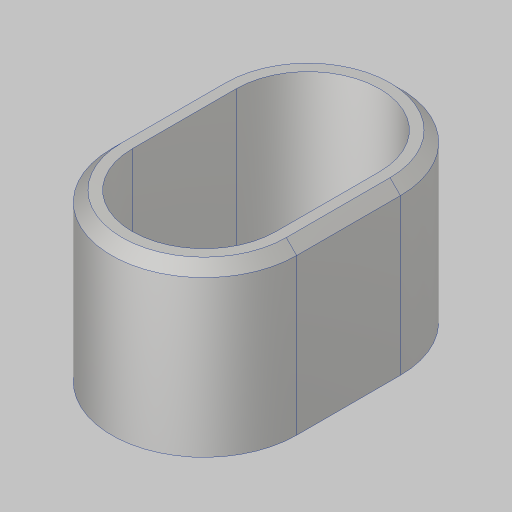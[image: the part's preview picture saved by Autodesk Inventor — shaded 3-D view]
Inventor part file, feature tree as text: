
AUTODESK INVENTOR PART (.ipt)
format: ipt  version: 2023.5 (Build 275446000, 446)  size: 137,216 bytes
history: native  units: in
note: dims shown in document units (in); Inventor stores cm internally (conversion verified against a paired STEP export)
features: sketch x1, extrude x1, chamfer x1
ambient origin geometry x8: Origin, YZ Plane, XZ Plane, XY Plane, X Axis, Y Axis, Z Axis, Center Point
bodies: Solid1 (feature_tree)
feature tree (3):
  sketch  "Sketch1"  dims[d1=1.375in d2=0.13in d3=2.0in d4=1.0in d5=0.0in d15=0.125in d16=0.0625in d17=0.125in d18=45.0deg d8=0.5in d9=0.0344in d10=0.5in d11=0.0344in]
  extrude  "Extrusion1"  Depth=0.5in
  chamfer  "Chamfer2"  Distance=2.0in
